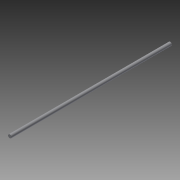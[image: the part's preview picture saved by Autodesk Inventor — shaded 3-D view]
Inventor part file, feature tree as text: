
AUTODESK INVENTOR PART (.ipt)
format: ipt  version: 2015 (Build 190159000, 159)  size: 65,024 bytes
history: native  units: mm
features: extrude x1, sketch x1
ambient origin geometry x8: Origin, YZ Plane, XZ Plane, XY Plane, X Axis, Y Axis, Z Axis, Center Point
bodies: Solid1 (feature_tree)
feature tree (2):
  extrude  "Extrusion1"  Depth=370.0mm TaperAngle=0.0deg
  sketch  "Sketch1"  dims[d0=8.0mm d1=370.0mm d2=0.0mm]
